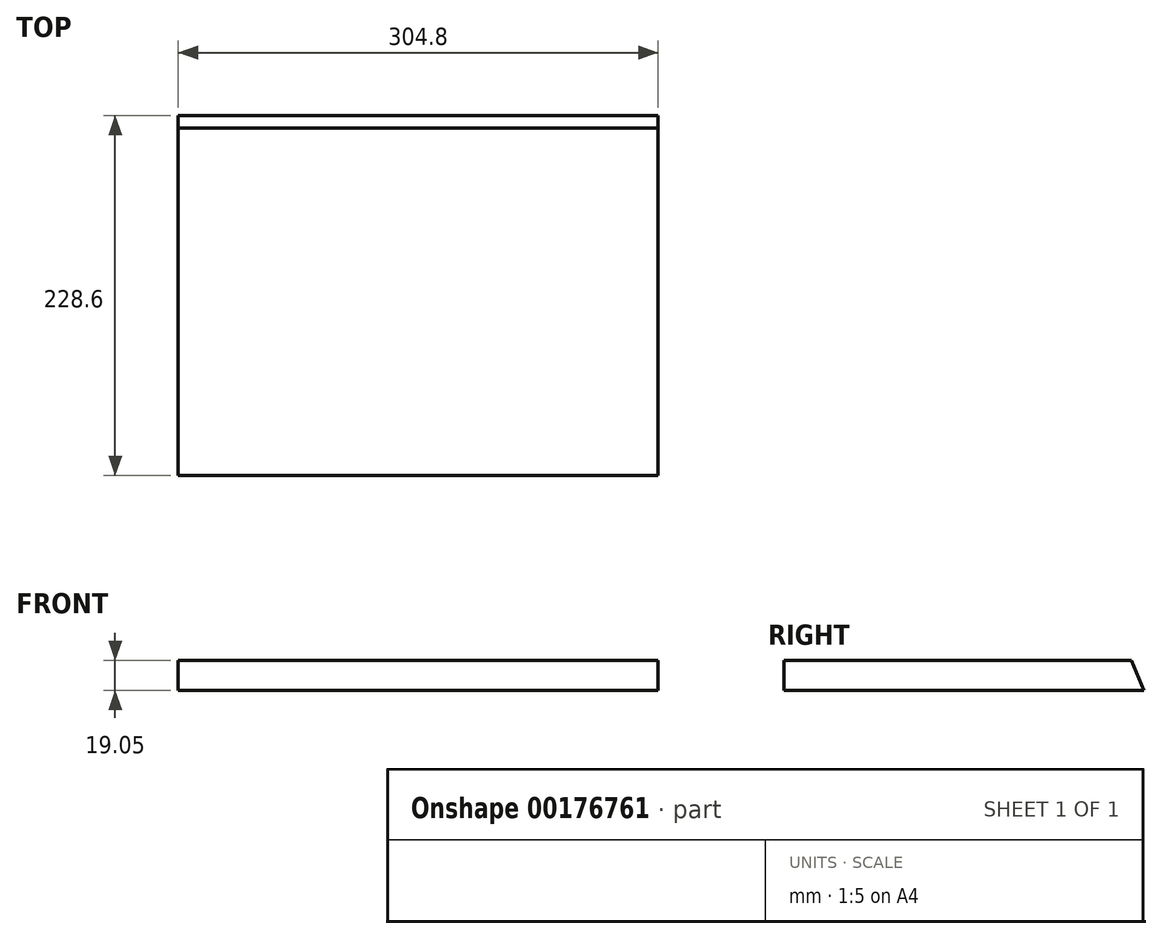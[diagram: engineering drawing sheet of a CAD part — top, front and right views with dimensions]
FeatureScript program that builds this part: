
annotation { "Feature Type Name" : "Feature", "Feature Type Description" : "" }
export const myFeature = defineFeature(function(context is Context, id is Id, definition is map)
    precondition{}
    {
        {
            var Q0;
            Q0=qCreatedBy(makeId("Top.planeOp"),FACE);
            var sketch = newSketch(context, id + "F0", { "sketchPlane" : qUnion([Q0])});
            skLineSegment(sketch, "E0.bottom", {"start": v(-152.4, 114.3) * mm, "end": v(152.4, 114.3) * mm});
            skLineSegment(sketch, "E0.top", {"start": v(-152.4, -114.3) * mm, "end": v(152.4, -114.3) * mm});
            skLineSegment(sketch, "E0.left", {"start": v(-152.4, 114.3) * mm, "end": v(-152.4, -114.3) * mm});
            skLineSegment(sketch, "E0.right", {"start": v(152.4, 114.3) * mm, "end": v(152.4, -114.3) * mm});
            skPoint(sketch, "E0.middle", {"position": v(0, 0) * mm});
            skSolve(sketch);
        }
        {
            var Q0;
            Q0=makeQuery(id+"F0.imprint","IMPRINT",FACE,{"disambiguationData":[TD([[makeQuery(id+"F0.imprint","IMPRINT",EDGE,{"derivedFrom":sQuery(id+"F0.wireOp",EDGE,"E0.bottom")}),-1.0]])]});
            extrude(context, id + "F1", {"entities" : qUnion([Q0]), "depth" : 19.05 * mm});
        }
        {
            var Q0;
            Q0=makeQuery(id+"F1.opExtrude","CAP_EDGE",EDGE,{"disambiguationData":[OSD([sQuery(id+"F0.wireOp",EDGE,"E0.bottom")])],"isStart":false});
            chamfer(context, id + "F2", {"entities" : qUnion([Q0]), "chamferType" : ChamferType.OFFSET_ANGLE, "width" : 19.05 * mm, "oppositeDirection" : false, "angle" : 22.5 * degree, "tangentPropagation" : true});
        }
    });
